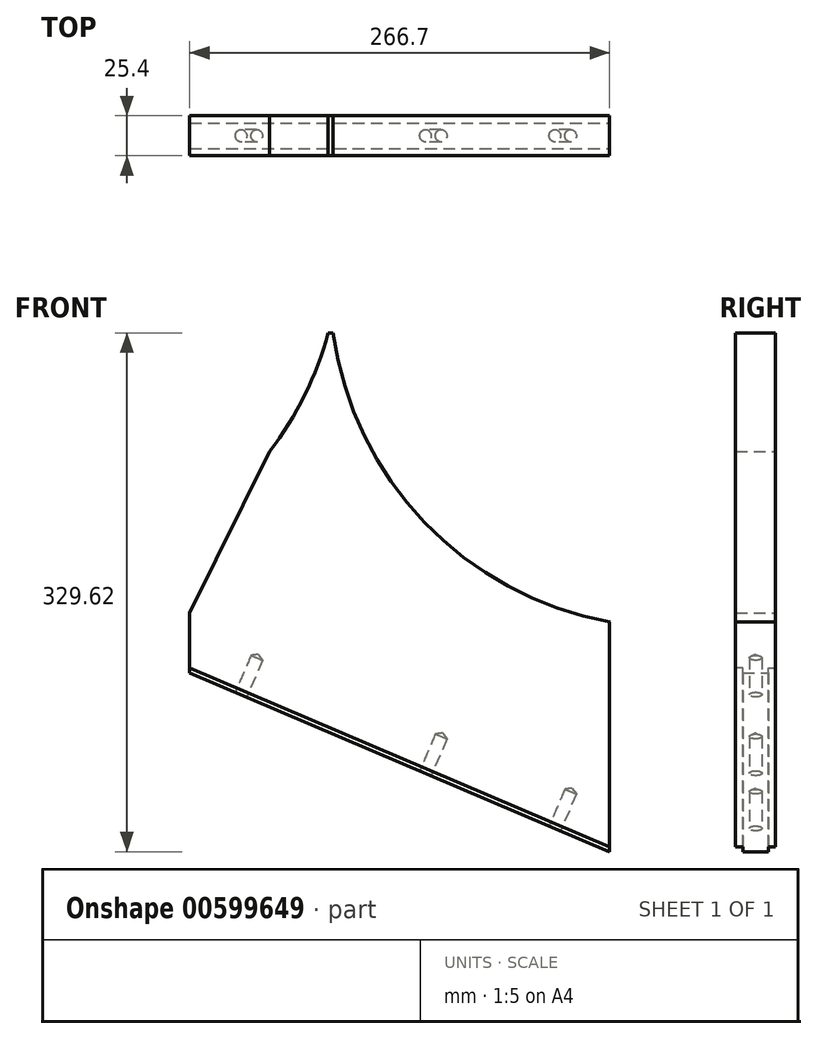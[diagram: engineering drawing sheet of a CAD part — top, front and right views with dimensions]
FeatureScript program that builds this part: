
annotation { "Feature Type Name" : "Feature", "Feature Type Description" : "" }
export const myFeature = defineFeature(function(context is Context, id is Id, definition is map)
    precondition{}
    {
        {
            var Q0;
            Q0=qCreatedBy(makeId("Front.planeOp"),FACE);
            var sketch = newSketch(context, id + "F0", { "sketchPlane" : qUnion([Q0])});
            skArc(sketch, "E0", {"start": v(91.1, 215.9) * mm, "mid": v(149.05, 95.59) * mm, "end": v(266.7, 32.38) * mm});
            skLineSegment(sketch, "E1", {"start": v(0, 0) * mm, "end": v(266.7, 0) * mm, "construction": true});
            skLineSegment(sketch, "E2", {"start": v(266.7, 32.38) * mm, "end": v(266.7, 0) * mm});
            skLineSegment(sketch, "E3", {"start": v(0, 0) * mm, "end": v(0, 38.1) * mm});
            skLineSegment(sketch, "E4", {"start": v(91.1, 215.9) * mm, "end": v(266.7, 32.38) * mm, "construction": true});
            skLineSegment(sketch, "E5", {"start": v(91.1, 215.9) * mm, "end": v(87.92, 215.9) * mm});
            skLineSegment(sketch, "E6", {"start": v(50.66, 140.56) * mm, "end": v(0, 38.1) * mm});
            skArc(sketch, "E7", {"start": v(50.66, 140.56) * mm, "mid": v(73, 176.4) * mm, "end": v(87.92, 215.9) * mm});
            skLineSegment(sketch, "E8", {"start": v(50.66, 140.56) * mm, "end": v(87.92, 215.9) * mm, "construction": true});
            skLineSegment(sketch, "E9.0", {"start": v(0, 0) * mm, "end": v(87.92, 0) * mm, "construction": true});
            skLineSegment(sketch, "E9.1", {"start": v(87.92, 0) * mm, "end": v(87.92, 215.9) * mm, "construction": true});
            skLineSegment(sketch, "E10", {"start": v(266.7, 32.38) * mm, "end": v(0, 32.38) * mm, "construction": true});
            skLineSegment(sketch, "E11.right", {"start": v(266.7, 0) * mm, "end": v(266.7, -113.72) * mm});
            skLineSegment(sketch, "E12", {"start": v(0, 0) * mm, "end": v(266.7, -113.72) * mm});
            skSolve(sketch);
        }
        {
            var Q0;
            Q0=makeQuery(id+"F0.imprint","IMPRINT",FACE,{"disambiguationData":[TD([[makeQuery(id+"F0.imprint","IMPRINT",EDGE,{"derivedFrom":sQuery(id+"F0.wireOp",EDGE,"E0")}),-1.0]])]});
            extrude(context, id + "F1", {"entities" : qUnion([Q0]), "depth" : 25.4 * mm, "offsetDistance" : 25.4 * mm});
        }
        {
            var Q0;
            Q0=makeQuery(id+"F1.opExtrude","SWEPT_FACE",FACE,{"disambiguationData":[OSD([sQuery(id+"F0.wireOp",EDGE,"E12")])]});
            var sketch = newSketch(context, id + "F2", { "sketchPlane" : qUnion([Q0])});
            skPoint(sketch, "E13", {"position": v(252.1, 12.7) * mm});
            skPoint(sketch, "E13.positionSnap0", {"position": v(289.93, 12.7) * mm});
            skPoint(sketch, "E14", {"position": v(162.72, 12.7) * mm});
            skPoint(sketch, "E15", {"position": v(35.41, 12.7) * mm});
            skSolve(sketch);
        }
        {
            var Q0;
            Q0=sQuery(id+"F2.wireOp",VERTEX,"E15");
            var Q1;
            Q1=sQuery(id+"F2.wireOp",VERTEX,"E14");
            var Q2;
            Q2=sQuery(id+"F2.wireOp",VERTEX,"E13");
            var Q3;
            Q3=makeQuery(id+"F1.opExtrude","SWEPT_BODY",BODY,{"disambiguationData":[OSD([sQuery(id+"F0.wireOp",EDGE,"H6WLdUrZ-ntxF-tdLD-nKnK-wzyLtiNqgXZ7"),sQuery(id+"F0.wireOp",EDGE,"E0"),sQuery(id+"F0.wireOp",EDGE,"E1"),sQuery(id+"F0.wireOp",EDGE,"E2"),sQuery(id+"F0.wireOp",EDGE,"E3")])]});
            hole(context, id + "F3", {"style" : HoleStyle.SIMPLE, "endStyle" : HoleEndStyle.BLIND, "standardTappedOrClearance" : lookupTablePath({ "standard" : "ANSI", "engagement" : "75%", "pitch" : "16 tpi", "size" : "3/8", "type" : "Tapped" }), "standardBlindInLast" : lookupTablePath({ "standard" : "ANSI", "engagement" : "75%", "pitch" : "16 tpi", "size" : "3/8", "type" : "Tapped" }), "holeDiameter" : 7.94 * mm, "majorDiameter" : 9.52 * mm, "showTappedDepth" : true, "holeDepth" : 25.4 * mm, "tappedDepth" : 20.64 * mm, "tapClearance" : 3, "startFromSketch" : true, "locations" : qUnion([Q0, Q1, Q2]), "scope" : qUnion([Q3])});
        }
        {
            var Q0;
            Q0=makeQuery(id+"F1.opExtrude","CAP_FACE",FACE,{"disambiguationData":[OSD([sQuery(id+"F0.wireOp",EDGE,"E0"),sQuery(id+"F0.wireOp",EDGE,"E2"),sQuery(id+"F0.wireOp",EDGE,"E3"),sQuery(id+"F0.wireOp",EDGE,"E5"),sQuery(id+"F0.wireOp",EDGE,"E6"),sQuery(id+"F0.wireOp",EDGE,"E7"),sQuery(id+"F0.wireOp",EDGE,"E11.right"),sQuery(id+"F0.wireOp",EDGE,"E12")])],"isStart":false});
            var sketch = newSketch(context, id + "F4", { "sketchPlane" : qUnion([Q0])});
            skLineSegment(sketch, "E16", {"start": v(0, 0) * mm, "end": v(266.7, -113.72) * mm});
            skLineSegment(sketch, "E17", {"start": v(266.7, -110.54) * mm, "end": v(0, 3.17) * mm});
            skLineSegment(sketch, "E18", {"start": v(0, 3.17) * mm, "end": v(0, 0) * mm});
            skLineSegment(sketch, "E19", {"start": v(266.7, -110.54) * mm, "end": v(266.7, -113.72) * mm});
            skSolve(sketch);
        }
        {
            var Q0;
            Q0=makeQuery(id+"F4.imprint","IMPRINT",FACE,{"disambiguationData":[TD([[makeQuery(id+"F4.imprint","IMPRINT",EDGE,{"derivedFrom":sQuery(id+"F4.wireOp",EDGE,"E16")}),1.0]])]});
            extrude(context, id + "F5", {"entities" : qUnion([Q0]), "operationType" : NewBodyOperationType.REMOVE, "oppositeDirection" : true, "depth" : 4.57 * mm, "offsetDistance" : 25.4 * mm});
        }
        {
            var Q0;
            Q0=makeQuery(id+"F1.opExtrude","CAP_FACE",FACE,{"disambiguationData":[OSD([sQuery(id+"F0.wireOp",EDGE,"E0"),sQuery(id+"F0.wireOp",EDGE,"E2"),sQuery(id+"F0.wireOp",EDGE,"E3"),sQuery(id+"F0.wireOp",EDGE,"E5"),sQuery(id+"F0.wireOp",EDGE,"E6"),sQuery(id+"F0.wireOp",EDGE,"E7"),sQuery(id+"F0.wireOp",EDGE,"E11.right"),sQuery(id+"F0.wireOp",EDGE,"E12")])],"isStart":true});
            var sketch = newSketch(context, id + "F6", { "sketchPlane" : qUnion([Q0])});
            skLineSegment(sketch, "E20", {"start": v(-266.7, -113.72) * mm, "end": v(0, 0) * mm});
            skLineSegment(sketch, "E21", {"start": v(-266.7, -113.72) * mm, "end": v(-266.7, -110.54) * mm});
            skLineSegment(sketch, "E22", {"start": v(-266.7, -110.54) * mm, "end": v(0, 3.17) * mm});
            skLineSegment(sketch, "E23", {"start": v(0, 3.17) * mm, "end": v(0, 0) * mm});
            skSolve(sketch);
        }
        {
            var Q0;
            Q0 = qSketchRegion(id + "F6", true);
            extrude(context, id + "F7", {"entities" : qUnion([Q0]), "operationType" : NewBodyOperationType.REMOVE, "oppositeDirection" : true, "depth" : 4.57 * mm, "offsetDistance" : 25.4 * mm});
        }
    });
